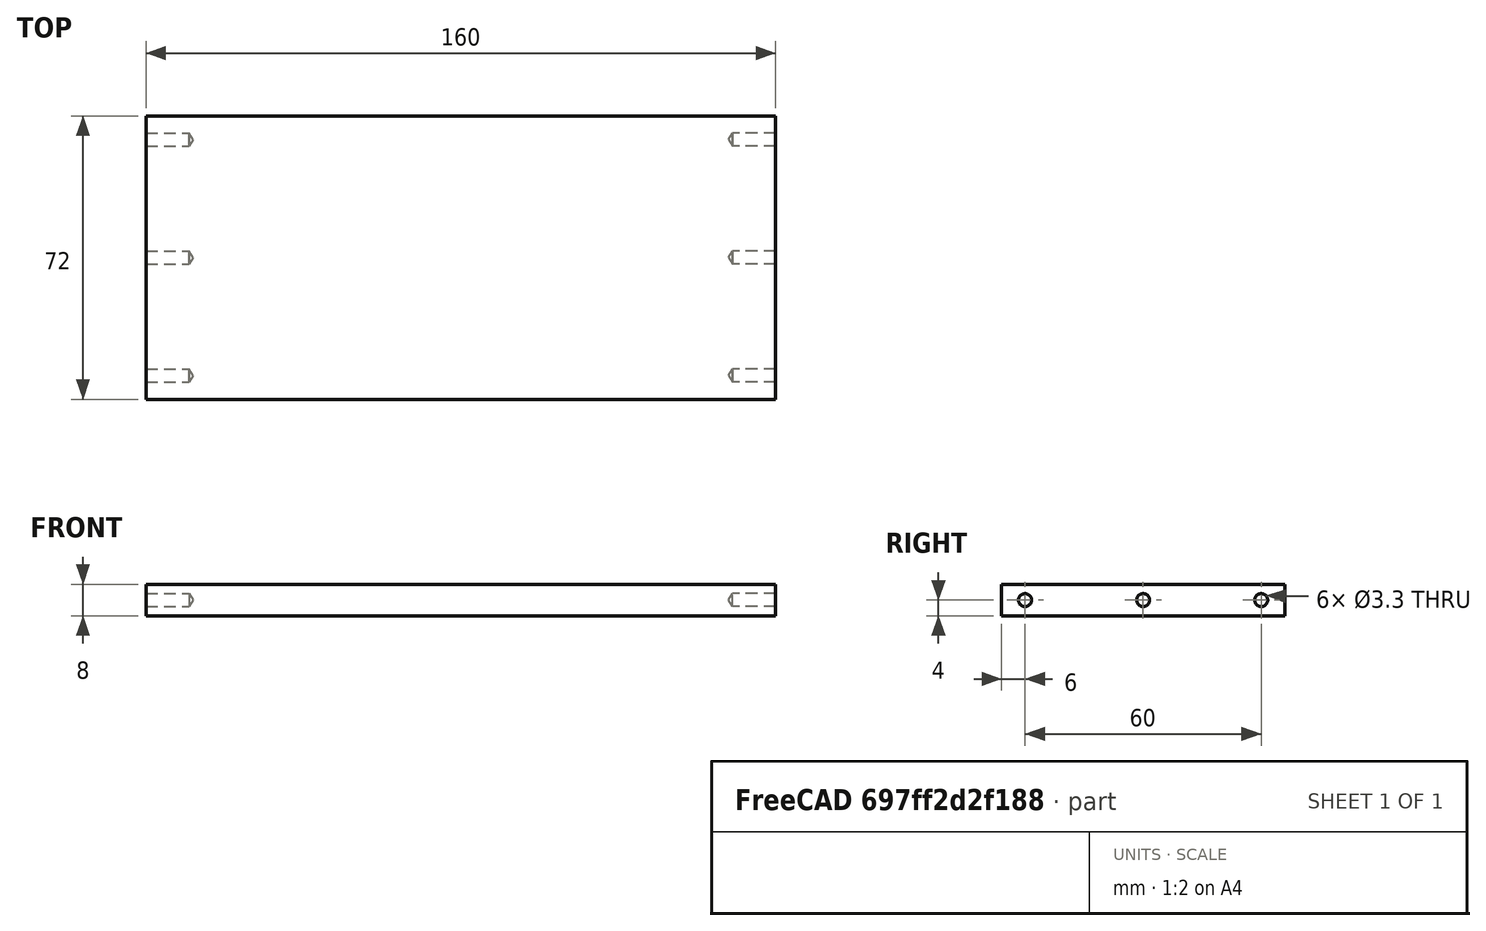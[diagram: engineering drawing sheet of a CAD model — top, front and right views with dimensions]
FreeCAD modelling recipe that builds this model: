
FCSTD DOCUMENT  (FreeCAD 0.17R13522 (Git))
Label: Boden
License: All rights reserved
LicenseURL: http://en.wikipedia.org/wiki/All_rights_reserved
objects: TechDraw::DrawViewDimension×8, TechDraw::DrawProjGroupItem×3, Sketcher::SketchObject×2, PartDesign::Hole×2, Part::Box×1, PartDesign::FeatureBase×1, PartDesign::Body×1, TechDraw::DrawSVGTemplate×1, TechDraw::DrawProjGroup×1, TechDraw::DrawViewAnnotation×1, TechDraw::DrawPage×1
note: 9 computed .brp shape members not serialized (recipe doc carries the construction recipe); baked Part::Feature solids carry a one-line shape summary decoded from their .brp

FEATURE [Part::Box] Box  label="Würfel"
  AttacherType = Attacher::AttachEngine3D
  Height = 8
  Length = 160
  Width = 72
FEATURE [PartDesign::FeatureBase] BaseFeature
  BaseFeature = -> Box
FEATURE [Sketcher::SketchObject] Sketch
  MapMode = 5
  Placement = pos=(0,0,0) rot=(0.57735,-0.57735,-0.57735;2.0944rad)
  Support = -> [BaseFeature]
  sketch-geometry (3):
    g0: Circle CenterX=-66 CenterY=4 CenterZ=0 NormalX=0 NormalY=0 NormalZ=1 AngleXU=0 Radius=2
    g1: Circle CenterX=-36 CenterY=4 CenterZ=0 NormalX=0 NormalY=0 NormalZ=1 AngleXU=0 Radius=2
    g2: Circle CenterX=-6 CenterY=4 CenterZ=0 NormalX=0 NormalY=0 NormalZ=1 AngleXU=0 Radius=2
  constraints (9):
    c: Radius(g2) = 2
    c: Radius(g1) = 2
    c: Radius(g0) = 2
    c: DistanceY(g-1,g2) = 4
    c: Horizontal(g0,g1)
    c: Horizontal(g1,g2)
    c: DistanceX(g2,g-1) = 6
    c: DistanceX(g1,g-1) = 36
    c: DistanceX(g0,g-1) = 66
FEATURE [PartDesign::Hole] Hole
  BaseFeature = -> BaseFeature
  Depth = 12
  DepthType = 0
  Diameter = 3.3
  DrillPoint = 1
  DrillPointAngle = 118
  HoleCutCountersinkAngle = 90
  HoleCutDepth = 0
  HoleCutDiameter = 4
  HoleCutType = 0
  ModelActualThread = false
  Profile = -> Sketch
  Tapered = false
  TaperedAngle = 90
  ThreadAngle = 60
  ThreadClass = 0
  ThreadCutOffInner = 0.0757772
  ThreadCutOffOuter = 0.151554
  ThreadDirection = 1
  ThreadFit = 0
  ThreadPitch = 0.7
  ThreadSize = 5
  ThreadType = 1
  Threaded = true
FEATURE [Sketcher::SketchObject] Sketch001
  MapMode = 5
  Placement = pos=(160,0,0) rot=(0.57735,0.57735,0.57735;2.0944rad)
  Support = -> [Hole]
  sketch-geometry (3):
    g0: Circle CenterX=6 CenterY=4 CenterZ=0 NormalX=0 NormalY=0 NormalZ=1 AngleXU=0 Radius=2
    g1: Circle CenterX=36 CenterY=4 CenterZ=0 NormalX=0 NormalY=0 NormalZ=1 AngleXU=0 Radius=2
    g2: Circle CenterX=66 CenterY=4 CenterZ=0 NormalX=0 NormalY=0 NormalZ=1 AngleXU=0 Radius=2
  constraints (9):
    c: Radius(g0) = 2
    c: Radius(g1) = 2
    c: Radius(g2) = 2
    c: Horizontal(g0,g1)
    c: Horizontal(g1,g2)
    c: DistanceY(g-1,g0) = 4
    c: DistanceX(g-1,g0) = 6
    c: DistanceX(g-1,g1) = 36
    c: DistanceX(g-1,g2) = 66
FEATURE [PartDesign::Hole] Hole001
  BaseFeature = -> Hole
  Depth = 12
  DepthType = 0
  Diameter = 3.3
  DrillPoint = 1
  DrillPointAngle = 118
  HoleCutCountersinkAngle = 90
  HoleCutDepth = 0
  HoleCutDiameter = 4
  HoleCutType = 0
  ModelActualThread = false
  Profile = -> Sketch001
  Tapered = false
  TaperedAngle = 90
  ThreadAngle = 60
  ThreadClass = 0
  ThreadCutOffInner = 0.0757772
  ThreadCutOffOuter = 0.151554
  ThreadDirection = 1
  ThreadFit = 0
  ThreadPitch = 0.7
  ThreadSize = 5
  ThreadType = 1
  Threaded = true
FEATURE [PartDesign::Body] Body
  BaseFeature = -> Box
  Group = -> [BaseFeature,Sketch,Hole,Sketch001,Hole001]
  Origin = -> Origin
  Tip = -> Hole001
FEATURE [TechDraw::DrawSVGTemplate] Template
  EditableTexts = Designed_by_Name=Christian; FC-Date=25.05.2018; FC-SC=1/1; FC-SH=1/1; FC-Title=Bodenplatte
  Height = 210
  Orientation = 1
  Width = 297
FEATURE [TechDraw::DrawProjGroupItem] ProjItem  label="Front"
  CoarseView = false
  Direction = (1,0,0)
  Focus = 100
  HardHidden = false
  IsoCount = 0
  IsoHidden = false
  IsoVisible = false
  LockPosition = false
  Perspective = false
  Rotation = 0
  RotationVector = (0,0,-1)
  ScaleType = 0
  SeamHidden = false
  SeamVisible = false
  SmoothHidden = false
  SmoothVisible = false
  Source = -> [Body]
  Type = 0
  X = -125.5
  Y = 0
FEATURE [TechDraw::DrawProjGroupItem] ProjItem001  label="Left"
  CoarseView = false
  Direction = (0,0,1)
  Focus = 100
  HardHidden = false
  IsoCount = 0
  IsoHidden = false
  IsoVisible = false
  LockPosition = true
  Perspective = false
  Rotation = 0
  RotationVector = (1,0,0)
  ScaleType = 0
  SeamHidden = false
  SeamVisible = false
  SmoothHidden = false
  SmoothVisible = false
  Source = -> [Body]
  Type = 1
  X = 144.552
  Y = 0
FEATURE [TechDraw::DrawProjGroupItem] ProjItem002  label="Rear"
  CoarseView = false
  Direction = (-1,0,0)
  Focus = 100
  HardHidden = false
  IsoCount = 0
  IsoHidden = false
  IsoVisible = false
  LockPosition = true
  Perspective = false
  Rotation = 0
  RotationVector = (0,0,1)
  ScaleType = 0
  SeamHidden = false
  SeamVisible = false
  SmoothHidden = false
  SmoothVisible = false
  Source = -> [Body]
  Type = 3
  X = 242.586
  Y = 0
FEATURE [TechDraw::DrawProjGroup] ProjGroup
  Anchor = -> ProjItem
  AutoDistribute = true
  CubeDirs = (6) [(-6.12323e-17,-1,-6.12323e-17),(1,-6.12323e-17,0),(-3.7494e-33,-6.12323e-17,1),(-1,6.12323e-17,0),(3.7494e-33,6.12323e-17,-1),(6.12323e-17,1,6.12323e-17)]
  CubeRotations = (6) [(1.22465e-16,-6.12323e-17,-1),(1.22465e-16,-6.12323e-17,-1),(1,6.12323e-17,0),(-1.22465e-16,6.12323e-17,1),(-1,-6.12323e-17,0),(1.22465e-16,-6.12323e-17,-1)]
  LockPosition = false
  ProjectionType = 0
  Rotation = 0
  ScaleType = 0
  Source = -> [Body]
  Views = -> [ProjItem,ProjItem001,ProjItem002]
  X = 26.1415
  Y = 147.421
  spacingX = 15
  spacingY = 15
FEATURE [TechDraw::DrawViewDimension] Dimension
  FormatSpec = %.2f
  LockPosition = false
  MeasureType = 1
  References2D = -> [ProjItem]
  Rotation = 0
  ScaleType = 0
  Type = 1
  X = 17.1252
  Y = -73.4698
FEATURE [TechDraw::DrawViewDimension] Dimension001
  FormatSpec = %.2f
  LockPosition = false
  MeasureType = 1
  References2D = -> [ProjItem]
  Rotation = 0
  ScaleType = 0
  Type = 2
  X = 12.7341
  Y = -50.9364
FEATURE [TechDraw::DrawViewDimension] Dimension002
  FormatSpec = %.2f
  LockPosition = false
  MeasureType = 1
  References2D = -> [ProjItem]
  Rotation = 0
  ScaleType = 0
  Type = 2
  X = 23.2341
  Y = -21.0001
FEATURE [TechDraw::DrawViewDimension] Dimension003
  FormatSpec = %.2f
  LockPosition = false
  MeasureType = 1
  References2D = -> [ProjItem]
  Rotation = 0
  ScaleType = 0
  Type = 2
  X = 30.765
  Y = -20.9642
FEATURE [TechDraw::DrawViewDimension] Dimension004
  FormatSpec = %.2f
  LockPosition = false
  MeasureType = 1
  References2D = -> [ProjItem]
  Rotation = 0
  ScaleType = 0
  Type = 5
  X = 31.0533
  Y = 44.0108
FEATURE [TechDraw::DrawViewDimension] Dimension005
  FormatSpec = %.2f
  LockPosition = false
  MeasureType = 1
  References2D = -> [ProjItem001]
  Rotation = 0
  ScaleType = 0
  Type = 1
  X = 2.93674
  Y = -59.6158
FEATURE [TechDraw::DrawViewDimension] Dimension006
  FormatSpec = %.2f
  LockPosition = false
  MeasureType = 1
  References2D = -> [ProjItem]
  Rotation = 0
  ScaleType = 0
  Type = 2
  X = 38.7649
  Y = -21.4382
FEATURE [TechDraw::DrawViewAnnotation] Annotation
  Font = osifont
  LineSpace = 80
  LockPosition = false
  MaxWidth = -1
  Rotation = 0
  ScaleType = 0
  Text = Bohrungen sind eig. | M4 Gewinde |  Tiefe ca 12mm 
  TextSize = 8
  TextStyle = 0
  X = 89.6247
  Y = 40.5269
FEATURE [TechDraw::DrawViewDimension] Dimension007
  FormatSpec = %.2f
  LockPosition = false
  MeasureType = 1
  References2D = -> [ProjItem]
  Rotation = 0
  ScaleType = 0
  Type = 1
  X = 17.3349
  Y = -65.8727
FEATURE [TechDraw::DrawPage] Page
  KeepUpdated = true
  ProjectionType = 0
  Template = -> Template
  Views = -> [ProjGroup,Dimension,Dimension001,Dimension002,Dimension003,Dimension004,Dimension005,Dimension006,Annotation,Dimension007]
